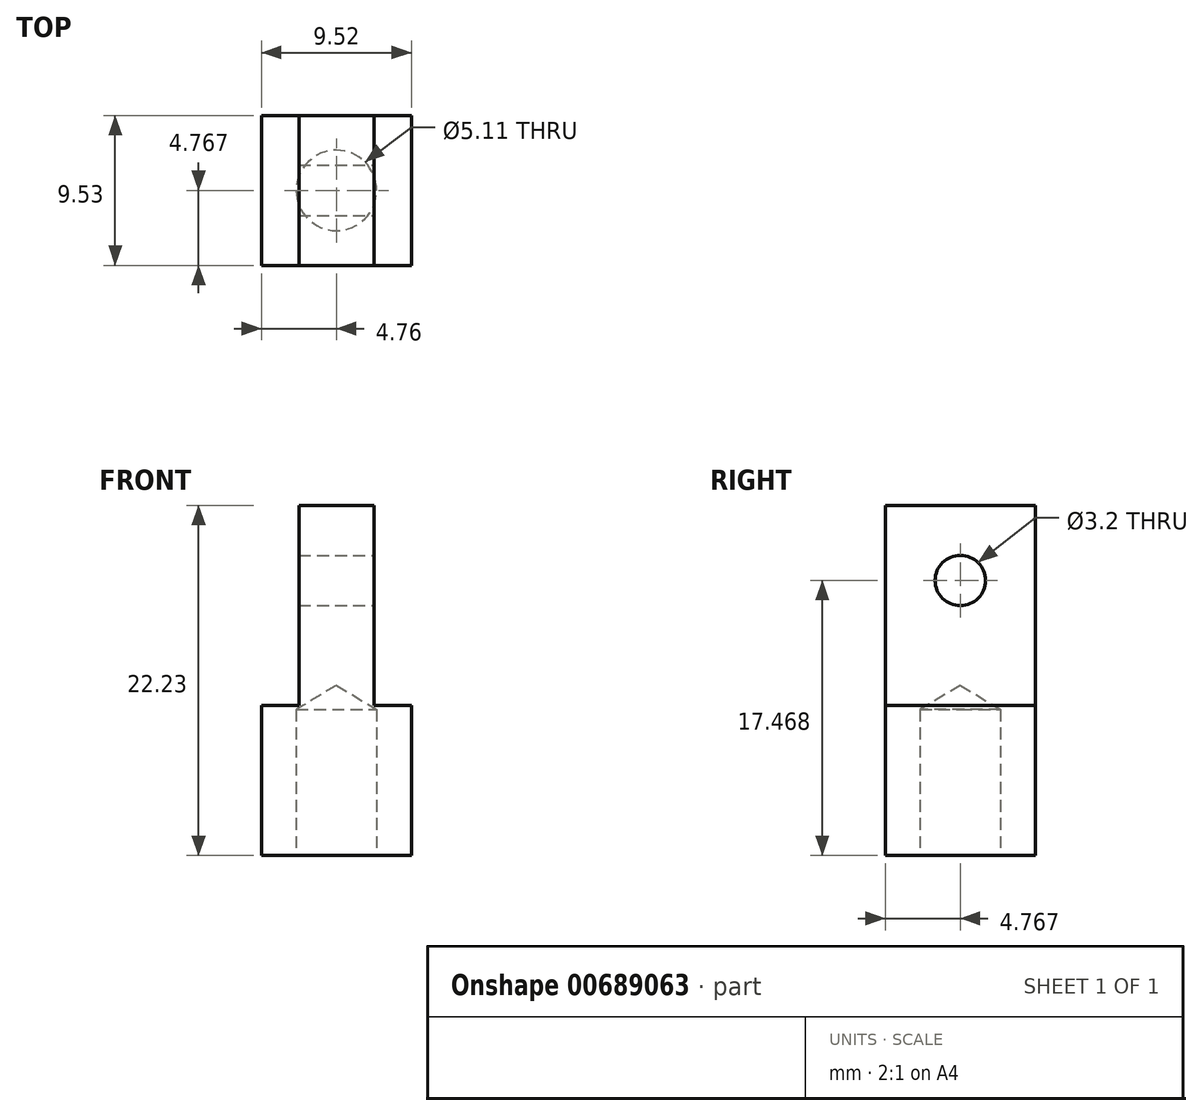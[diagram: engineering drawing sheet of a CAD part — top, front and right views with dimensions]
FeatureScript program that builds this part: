
annotation { "Feature Type Name" : "Feature", "Feature Type Description" : "" }
export const myFeature = defineFeature(function(context is Context, id is Id, definition is map)
    precondition{}
    {
        {
            var Q0;
            Q0=qCreatedBy(makeId("Front.planeOp"),FACE);
            var sketch = newSketch(context, id + "F0", { "sketchPlane" : qUnion([Q0])});
            skLineSegment(sketch, "E0.bottom", {"start": v(0, 0) * mm, "end": v(-4.76, 0) * mm});
            skLineSegment(sketch, "E0.top", {"start": v(0, -9.53) * mm, "end": v(-4.76, -9.53) * mm});
            skLineSegment(sketch, "E0.left", {"start": v(0, 0) * mm, "end": v(0, -9.53) * mm});
            skLineSegment(sketch, "E0.right", {"start": v(-4.76, 0) * mm, "end": v(-4.76, -9.53) * mm});
            skLineSegment(sketch, "E1.MirrorCS", {"start": v(0, -9.53) * mm, "end": v(4.76, -9.53) * mm});
            skLineSegment(sketch, "E2.MirrorCS", {"start": v(4.76, 0) * mm, "end": v(4.76, -9.53) * mm});
            skLineSegment(sketch, "E3.MirrorCS", {"start": v(0, 0) * mm, "end": v(4.76, 0) * mm});
            skLineSegment(sketch, "E4.bottom", {"start": v(0, 0) * mm, "end": v(-2.38, 0) * mm});
            skLineSegment(sketch, "E4.top", {"start": v(0, 12.7) * mm, "end": v(-2.38, 12.7) * mm});
            skLineSegment(sketch, "E4.left", {"start": v(0, 0) * mm, "end": v(0, 12.7) * mm});
            skLineSegment(sketch, "E4.right", {"start": v(-2.38, 0) * mm, "end": v(-2.38, 12.7) * mm});
            skLineSegment(sketch, "E5.MirrorCS", {"start": v(2.38, 0) * mm, "end": v(2.38, 12.7) * mm});
            skLineSegment(sketch, "E6.MirrorCS", {"start": v(0, 12.7) * mm, "end": v(2.38, 12.7) * mm});
            skSolve(sketch);
        }
        {
            var Q0;
            Q0 = qSketchRegion(id + "F0", true);
            extrude(context, id + "F1", {"entities" : qUnion([Q0]), "depth" : 9.52 * mm, "offsetDistance" : 25.4 * mm});
        }
        {
            var Q0;
            Q0=makeQuery(id+"F1.opExtrude","SWEPT_FACE",FACE,{"disambiguationData":[OSD([sQuery(id+"F0.wireOp",EDGE,"E5.MirrorCS")])]});
            var sketch = newSketch(context, id + "F2", { "sketchPlane" : qUnion([Q0])});
            skLineSegment(sketch, "E7", {"start": v(-9.53, 7.94) * mm, "end": v(0, 7.94) * mm, "construction": true});
            skPoint(sketch, "E8", {"position": v(-4.76, 7.94) * mm});
            skSolve(sketch);
        }
        {
            var Q0;
            Q0=sQuery(id+"F2.wireOp",VERTEX,"E8");
            var Q1;
            Q1=makeQuery(id+"F1.opExtrude","SWEPT_BODY",BODY,{"disambiguationData":[OSD([sQuery(id+"F0.wireOp",EDGE,"E0.bottom"),sQuery(id+"F0.wireOp",EDGE,"E0.top"),sQuery(id+"F0.wireOp",EDGE,"E0.right"),sQuery(id+"F0.wireOp",EDGE,"E1.MirrorCS"),sQuery(id+"F0.wireOp",EDGE,"E2.MirrorCS"),sQuery(id+"F0.wireOp",EDGE,"E3.MirrorCS"),sQuery(id+"F0.wireOp",EDGE,"E4.top"),sQuery(id+"F0.wireOp",EDGE,"E4.right"),sQuery(id+"F0.wireOp",EDGE,"E5.MirrorCS"),sQuery(id+"F0.wireOp",EDGE,"E6.MirrorCS")])]});
            hole(context, id + "F3", {"style" : HoleStyle.SIMPLE, "endStyle" : HoleEndStyle.THROUGH, "holeDiameter" : 3.2 * mm, "majorDiameter" : 6.35 * mm, "isTappedThrough" : true, "tappedDepth" : 6.35 * mm, "tapClearance" : 3, "startFromSketch" : true, "locations" : qUnion([Q0]), "scope" : qUnion([Q1])});
        }
        {
            var Q0;
            Q0=makeQuery(id+"F1.opExtrude","SWEPT_FACE",FACE,{"disambiguationData":[OSD([sQuery(id+"F0.wireOp",EDGE,"E0.top"),sQuery(id+"F0.wireOp",EDGE,"E1.MirrorCS")])]});
            var sketch = newSketch(context, id + "F4", { "sketchPlane" : qUnion([Q0])});
            skLineSegment(sketch, "E9", {"start": v(0, 9.53) * mm, "end": v(0, 0) * mm, "construction": true});
            skPoint(sketch, "E10", {"position": v(0, 4.76) * mm});
            skSolve(sketch);
        }
        {
            var Q0;
            Q0=sQuery(id+"F4.wireOp",VERTEX,"E10");
            var Q1;
            Q1=makeQuery(id+"F1.opExtrude","SWEPT_BODY",BODY,{"disambiguationData":[OSD([sQuery(id+"F0.wireOp",EDGE,"E0.bottom"),sQuery(id+"F0.wireOp",EDGE,"E0.top"),sQuery(id+"F0.wireOp",EDGE,"E0.right"),sQuery(id+"F0.wireOp",EDGE,"E1.MirrorCS"),sQuery(id+"F0.wireOp",EDGE,"E2.MirrorCS"),sQuery(id+"F0.wireOp",EDGE,"E3.MirrorCS"),sQuery(id+"F0.wireOp",EDGE,"E4.top"),sQuery(id+"F0.wireOp",EDGE,"E4.right"),sQuery(id+"F0.wireOp",EDGE,"E5.MirrorCS"),sQuery(id+"F0.wireOp",EDGE,"E6.MirrorCS")])]});
            hole(context, id + "F5", {"style" : HoleStyle.SIMPLE, "endStyle" : HoleEndStyle.BLIND, "standardTappedOrClearance" : lookupTablePath({ "standard" : "ANSI", "engagement" : "75%", "pitch" : "20 tpi", "size" : "1/4", "type" : "Tapped" }), "standardBlindInLast" : lookupTablePath({ "standard" : "ANSI", "engagement" : "75%", "pitch" : "20 tpi", "size" : "1/4", "type" : "Tapped" }), "holeDiameter" : 5.1 * mm, "majorDiameter" : 6.35 * mm, "showTappedDepth" : true, "holeDepth" : 9.27 * mm, "isTappedThrough" : true, "tappedDepth" : 5.46 * mm, "tapClearance" : 3, "startFromSketch" : true, "locations" : qUnion([Q0]), "scope" : qUnion([Q1])});
        }
    });
